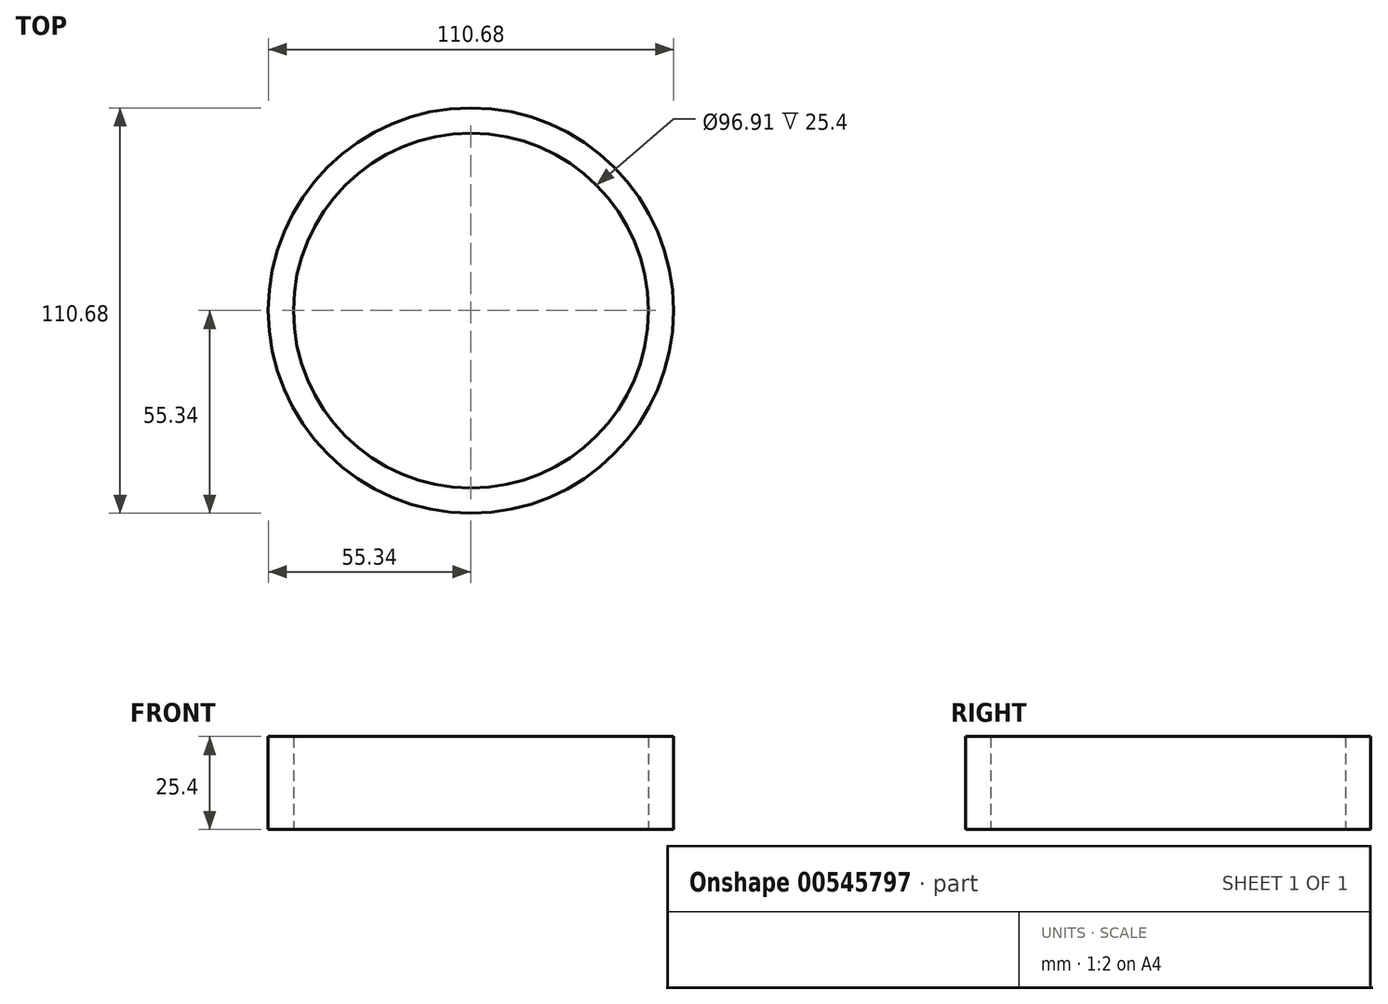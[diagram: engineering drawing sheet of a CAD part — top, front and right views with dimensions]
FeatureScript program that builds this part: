
annotation { "Feature Type Name" : "Feature", "Feature Type Description" : "" }
export const myFeature = defineFeature(function(context is Context, id is Id, definition is map)
    precondition{}
    {
        {
            var Q0;
            Q0=qCreatedBy(makeId("Top.planeOp"),FACE);
            var sketch = newSketch(context, id + "F0", { "sketchPlane" : qUnion([Q0])});
            skCircle(sketch, "E0", {"center": v(0, 0) * mm, "radius": 48.45 * mm});
            skLineSegment(sketch, "E1", {"start": v(0, 48.45) * mm, "end": v(0, 0) * mm});
            skLineSegment(sketch, "E2", {"start": v(0, -48.45) * mm, "end": v(0, 0) * mm});
            skLineSegment(sketch, "E3", {"start": v(0, 0) * mm, "end": v(48.45, 0) * mm});
            skLineSegment(sketch, "E4", {"start": v(-48.45, 0) * mm, "end": v(0, 0) * mm});
            skPoint(sketch, "E4.startSnap0", {"position": v(24.23, 0) * mm});
            skLineSegment(sketch, "E5", {"start": v(-33.62, 34.89) * mm, "end": v(0, 0) * mm});
            skLineSegment(sketch, "E6", {"start": v(0, 0) * mm, "end": v(34.9, -33.62) * mm});
            skLineSegment(sketch, "E7", {"start": v(-35.54, -32.93) * mm, "end": v(0, 0) * mm});
            skLineSegment(sketch, "E8", {"start": v(0, 0) * mm, "end": v(33.62, 34.9) * mm});
            skCircle(sketch, "E9", {"center": v(0, 0) * mm, "radius": 55.34 * mm});
            skSolve(sketch);
        }
        {
            var Q0;
            Q0 = qSketchRegion(id + "F0", true);
            extrude(context, id + "F1", {"entities" : qUnion([Q0]), "depth" : 25.4 * mm, "offsetDistance" : 25.4 * mm});
        }
    });
